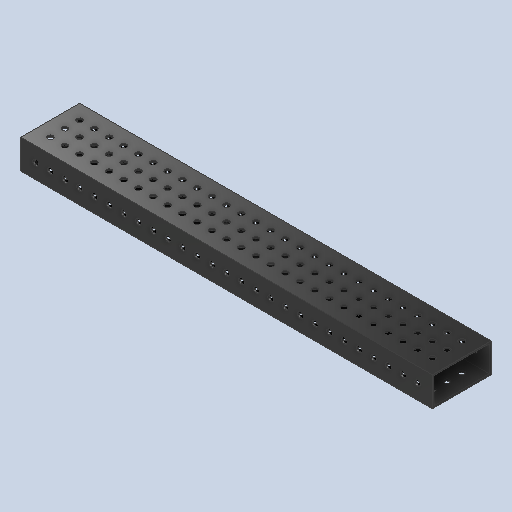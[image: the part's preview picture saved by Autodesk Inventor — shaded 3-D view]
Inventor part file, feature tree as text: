
AUTODESK INVENTOR PART (.ipt)
format: ipt  version: 2024 (Build 280153000, 153)  size: 415,232 bytes
history: native  units: in
note: dims shown in document units (in); Inventor stores cm internally (conversion verified against a paired STEP export)
features: other x4, extrude x1, sketch x1
ambient origin geometry x8: Origin, YZ Plane, XZ Plane, XY Plane, X Axis, Y Axis, Z Axis, Center Point
bodies: Body1 (feature_tree)
feature tree (6):
  other  "2024-220-000-Hard-Stop.ipt"
  extrude  "Extrusion1"  Depth=0.3937in
  other  "2024-220-002-Shootaur-Rest::2024-220-000-Hard-Stop.ipt"
  other  "TaggingFeature1"
  sketch  "Sketch1"  dims[d0=0.3937in d1=0.196in d2=0.5in d3=0.5in d4=1.1811in d6=0.5in d7=10.6299in d9=0.5in d12=1.1875in d13=0.0in]
  other  "2024-220-002-Shootaur-Rest"
